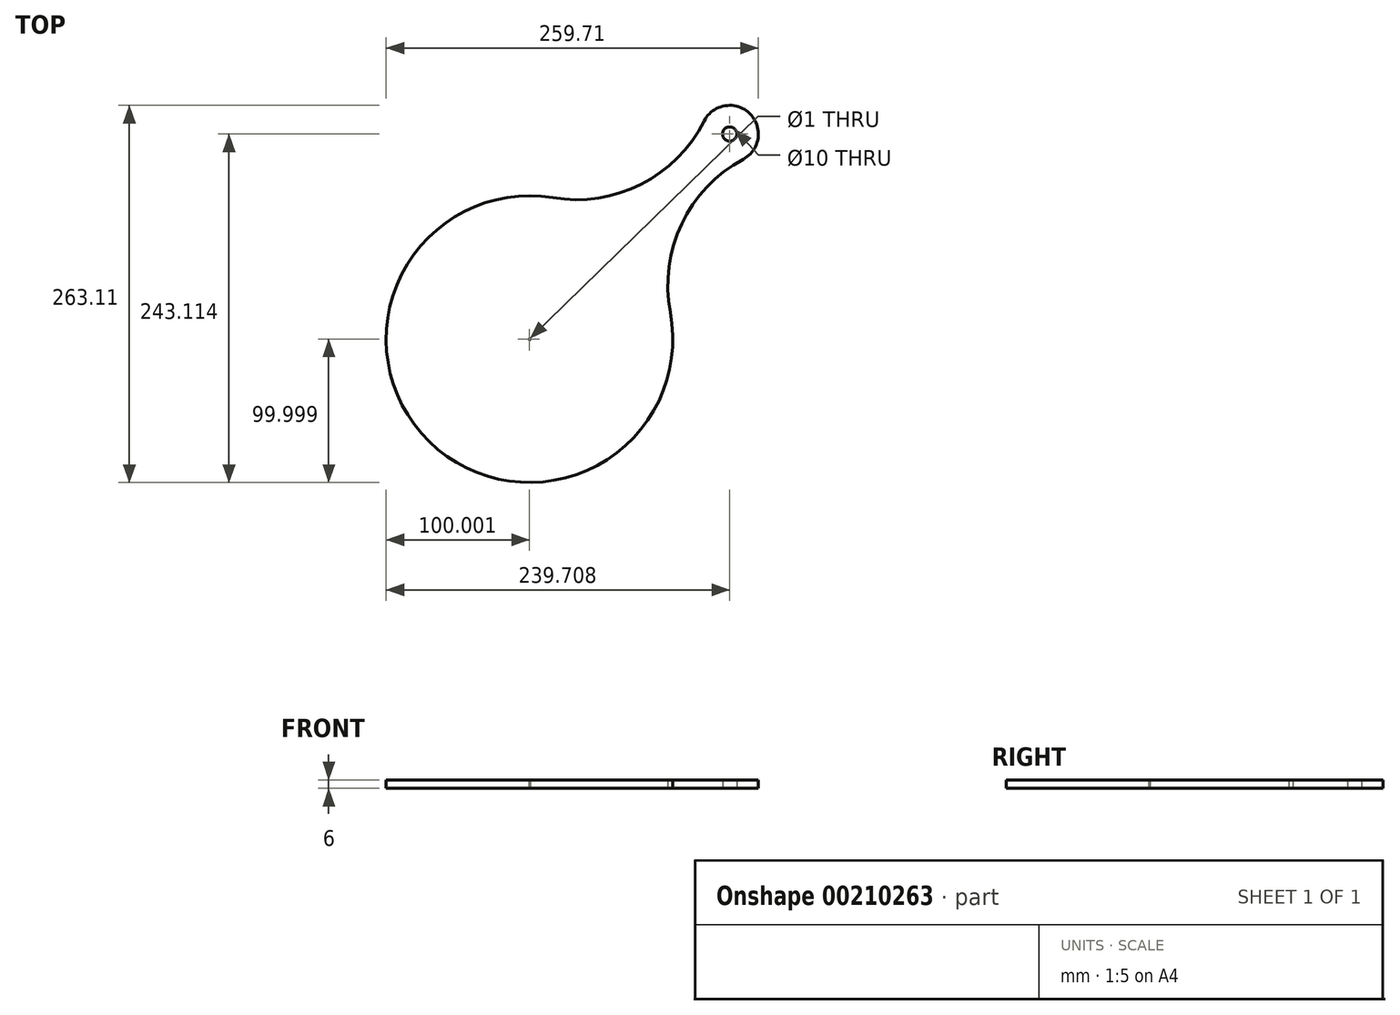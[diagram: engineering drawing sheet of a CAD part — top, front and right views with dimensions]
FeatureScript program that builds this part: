
annotation { "Feature Type Name" : "Feature", "Feature Type Description" : "" }
export const myFeature = defineFeature(function(context is Context, id is Id, definition is map)
    precondition{}
    {
        {
            var Q0;
            Q0=qCreatedBy(makeId("Top.planeOp"),FACE);
            var sketch = newSketch(context, id + "F0", { "sketchPlane" : qUnion([Q0])});
            skLineSegment(sketch, "E0.bottom", {"start": v(205, -210) * mm, "end": v(-205, -210) * mm});
            skLineSegment(sketch, "E0.top", {"start": v(205, 210) * mm, "end": v(-205, 210) * mm});
            skLineSegment(sketch, "E0.left", {"start": v(205, -210) * mm, "end": v(205, 210) * mm});
            skLineSegment(sketch, "E0.right", {"start": v(-205, -210) * mm, "end": v(-205, 210) * mm});
            skPoint(sketch, "E0.middle", {"position": v(0, 0) * mm});
            skSolve(sketch);
        }
        {
            var Q0;
            Q0=qCreatedBy(makeId("Top.planeOp"),FACE);
            var sketch = newSketch(context, id + "F1", { "sketchPlane" : qUnion([Q0])});
            skLineSegment(sketch, "E1", {"start": v(205, 210) * mm, "end": v(-205, -210) * mm, "construction": true});
            skCircle(sketch, "E2", {"center": v(-44.76, -45.85) * mm, "radius": 100 * mm});
            skCircle(sketch, "E3", {"center": v(94.95, 97.26) * mm, "radius": 20 * mm});
            skArc(sketch, "E4", {"start": v(104.4, 79.64) * mm, "mid": v(61.45, 34.58) * mm, "end": v(53.48, -27.16) * mm});
            skArc(sketch, "E5", {"start": v(-28.44, 52.8) * mm, "mid": v(33.1, 62.27) * mm, "end": v(77.1, 106.3) * mm});
            skCircle(sketch, "E6", {"center": v(-44.76, -45.85) * mm, "radius": 0.5 * mm});
            skCircle(sketch, "E7", {"center": v(94.95, 97.26) * mm, "radius": 5 * mm});
            skLineSegment(sketch, "E8", {"start": v(138.3, 162.4) * mm, "end": v(-196.76, -180.84) * mm, "construction": true});
            skLineSegment(sketch, "E9", {"start": v(186.98, 170.82) * mm, "end": v(-147.73, -172.05) * mm, "construction": true});
            skLineSegment(sketch, "E10", {"start": v(-147.73, -172.05) * mm, "end": v(-144.38, -175.32) * mm, "construction": true});
            skLineSegment(sketch, "E11", {"start": v(-168.8, -64.5) * mm, "end": v(-53.93, -176.64) * mm, "construction": true});
            skLineSegment(sketch, "E12", {"start": v(66.15, 153.32) * mm, "end": v(157.56, 64.09) * mm, "construction": true});
            skLineSegment(sketch, "E13", {"start": v(157.56, 64.09) * mm, "end": v(155.96, 62.44) * mm, "construction": true});
            skSolve(sketch);
        }
        {
            var Q0;
            Q0 = qSketchRegion(id + "F1", true);
            extrude(context, id + "F2", {"entities" : qUnion([Q0]), "depth" : 6 * mm});
        }
    });
